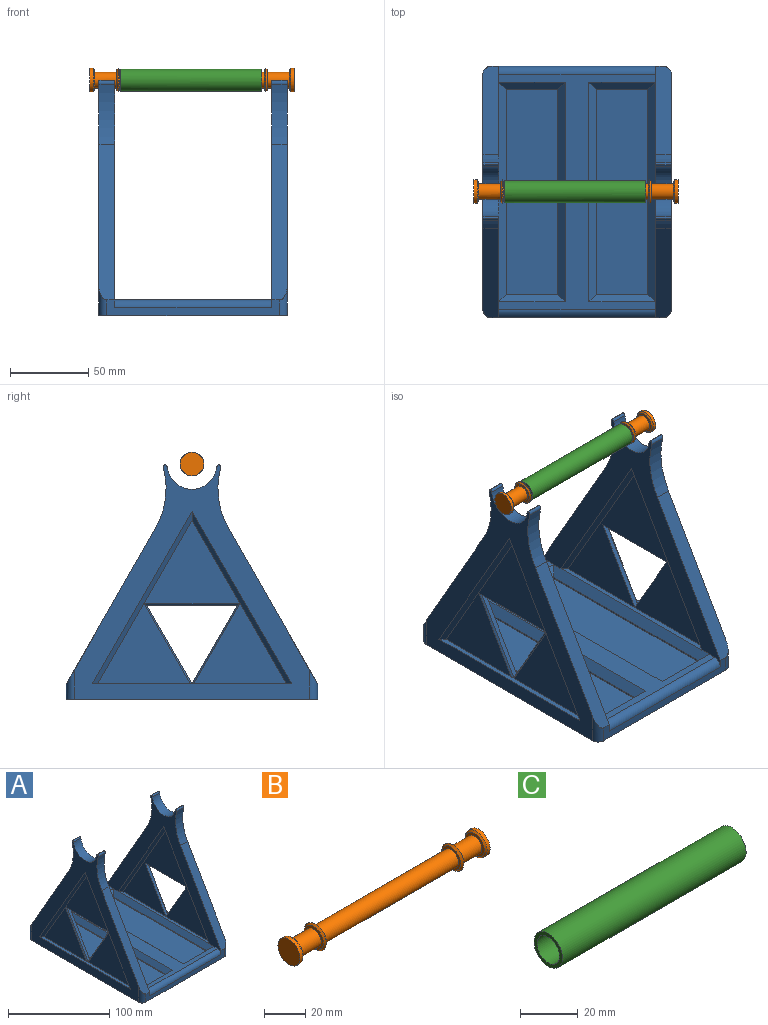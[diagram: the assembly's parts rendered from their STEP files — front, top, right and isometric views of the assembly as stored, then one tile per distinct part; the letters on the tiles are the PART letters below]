
ASSEMBLY  parts=3 mates=2
PART A: 82 faces, bbox 120x160x149.8 mm
  f0: plane 127.02x3mm, normal (0,0,1), area 370.7mm2, adj f25,f26,f27,f73
  f1: plane 127.02x3mm, normal (0,0,1), area 370.7mm2, adj f52,f53,f54,f78
  f2: plane 150x100mm, normal (0,0,1), area 3100mm2, adj f10,f41,f72,f74,f75,f76,f77,f79
  f3: plane 127.02x4mm, normal (0,0,1), area 371.8mm2, adj f13,f36,f51,f55,f56,f58,f59
  f4: plane 58.89x51mm, normal (1,0,0), area 1501.7mm2, adj f29,f32,f35
  f5: plane 61.2x53mm, normal (1,0,0), area 1621.8mm2, adj f28,f29,f30
  f6: plane 57.74x3mm, normal (0,0,-1), area 173.2mm2, adj f7,f8,f25,f30
  f7: plane 50x28.87mm, normal (0,-0.87,0.5), area 173.2mm2, adj f6,f8,f25,f32
  f8: plane 50x28.87mm, normal (0,0.87,0.5), area 173.2mm2, adj f6,f7,f25,f31
  f9: plane 150x149.84mm, normal (1,0,0), area 5795.8mm2, adj f14,f15,f16,f17,f18,f19,f20,f21
  f10: plane 160x144.84mm, normal (-1,0,0), area 4350.2mm2, adj f2,f11,f12,f15,f16,f17,f18,f19
  f11: plane 110x10mm, normal (0,-1,0), area 600mm2, adj f10,f14,f15,f33,f41,f42,f60,f81
  f12: plane 110x10mm, normal (0,1,0), area 600mm2, adj f10,f14,f16,f34,f41,f43,f61,f80
  f13: plane 150x149.84mm, normal (-1,0,0), area 5795.8mm2, adj f3,f14,f42,f43,f44,f45,f46,f47
  f14: plane 160x120mm, normal (0,0,-1), area 19178.5mm2, adj f9,f11,f12,f13,f33,f34,f60,f61
  f15: plane 99x56.57mm, normal (0,-0.87,0.5), area 1129.4mm2, adj f9,f10,f11,f19,f33
  f16: plane 99x56.57mm, normal (0,0.87,0.5), area 1129.4mm2, adj f9,f10,f12,f17,f34
  f17: cylinder r=50mm len=38.48mm, axis (1,0,0), area 398.7mm2, adj f9,f10,f16,f21
  f18: cylinder r=16mm len=31.8mm, axis (1,0,0), area 467mm2, adj f9,f10,f20,f23
  f19: cylinder r=50mm len=38.48mm, axis (1,0,0), area 398.7mm2, adj f9,f10,f15,f22
  f20: cylinder r=2mm len=10mm, axis (1,0,0), area 21.1mm2, adj f9,f10,f18,f21
  f21: cylinder r=2mm len=10mm, axis (1,0,0), area 28.6mm2, adj f9,f10,f17,f20
  f22: cylinder r=2mm len=10mm, axis (1,0,0), area 28.6mm2, adj f9,f10,f19,f23
  f23: cylinder r=2mm len=10mm, axis (1,0,0), area 21.1mm2, adj f9,f10,f18,f22
  f24: plane 58.89x51mm, normal (1,0,0), area 1501.7mm2, adj f28,f31,f35
  f25: plane 120.09x104mm, normal (-1,0,0), area 4801.2mm2, adj f0,f6,f7,f8,f26,f27
  f26: plane 110x63.51mm, normal (-0.71,-0.61,-0.35), area 524.2mm2, adj f0,f10,f25,f27
  f27: plane 110x63.51mm, normal (-0.71,0.61,-0.35), area 524.2mm2, adj f0,f10,f25,f26
  f28: plane 110x63.51mm, normal (0.71,0.61,-0.35), area 524.2mm2, adj f5,f9,f24,f29,f35
  f29: plane 110x63.51mm, normal (0.71,-0.61,-0.35), area 524.2mm2, adj f4,f5,f9,f28,f35
  f30: plane 61.2x1mm, normal (0.71,0,-0.71), area 84.1mm2, adj f5,f6,f31,f32
  f31: plane 51x30.6mm, normal (0.71,0.61,0.35), area 82.5mm2, adj f8,f24,f30,f35
  f32: plane 51x30.6mm, normal (0.71,-0.61,0.35), area 82.5mm2, adj f4,f7,f30,f35
  f33: cylinder r=5mm len=18.75mm, axis (0,0,-1), area 103.5mm2, adj f9,f11,f14,f15
  f34: cylinder r=5mm len=18.75mm, axis (0,0,1), area 103.5mm2, adj f9,f12,f14,f16
  f35: plane 127.02x4mm, normal (0,0,1), area 371.8mm2, adj f4,f9,f24,f28,f29,f31,f32
  f36: plane 58.89x51mm, normal (-1,0,0), area 1501.7mm2, adj f3,f56,f59
  f37: plane 61.2x53mm, normal (-1,0,0), area 1621.8mm2, adj f55,f56,f57
  f38: plane 57.74x3mm, normal (0,0,-1), area 173.2mm2, adj f39,f40,f52,f57
  f39: plane 50x28.87mm, normal (0,-0.87,0.5), area 173.2mm2, adj f38,f40,f52,f59
  f40: plane 50x28.87mm, normal (0,0.87,0.5), area 173.2mm2, adj f38,f39,f52,f58
  f41: plane 160x144.84mm, normal (1,0,0), area 4350.2mm2, adj f2,f11,f12,f42,f43,f44,f45,f46
  f42: plane 99x56.57mm, normal (0,-0.87,0.5), area 1129.4mm2, adj f11,f13,f41,f46,f60
  f43: plane 99x56.57mm, normal (0,0.87,0.5), area 1129.4mm2, adj f12,f13,f41,f44,f61
  f44: cylinder r=50mm len=38.48mm, axis (-1,0,0), area 398.7mm2, adj f13,f41,f43,f48
  f45: cylinder r=16mm len=31.8mm, axis (-1,0,0), area 467mm2, adj f13,f41,f47,f50
  f46: cylinder r=50mm len=38.48mm, axis (-1,0,0), area 398.7mm2, adj f13,f41,f42,f49
  f47: cylinder r=2mm len=10mm, axis (-1,0,0), area 21.1mm2, adj f13,f41,f45,f48
  f48: cylinder r=2mm len=10mm, axis (-1,0,0), area 28.6mm2, adj f13,f41,f44,f47
  f49: cylinder r=2mm len=10mm, axis (-1,0,0), area 28.6mm2, adj f13,f41,f46,f50
  f50: cylinder r=2mm len=10mm, axis (-1,0,0), area 21.1mm2, adj f13,f41,f45,f49
  f51: plane 58.89x51mm, normal (-1,0,0), area 1501.7mm2, adj f3,f55,f58
  f52: plane 120.09x104mm, normal (1,0,0), area 4801.2mm2, adj f1,f38,f39,f40,f53,f54
  f53: plane 110x63.51mm, normal (0.71,-0.61,-0.35), area 524.2mm2, adj f1,f41,f52,f54
  f54: plane 110x63.51mm, normal (0.71,0.61,-0.35), area 524.2mm2, adj f1,f41,f52,f53
  f55: plane 110x63.51mm, normal (-0.71,0.61,-0.35), area 524.2mm2, adj f3,f13,f37,f51,f56
  f56: plane 110x63.51mm, normal (-0.71,-0.61,-0.35), area 524.2mm2, adj f3,f13,f36,f37,f55
  f57: plane 61.2x1mm, normal (-0.71,0,-0.71), area 84.1mm2, adj f37,f38,f58,f59
  f58: plane 51x30.6mm, normal (-0.71,0.61,0.35), area 82.5mm2, adj f3,f40,f51,f57
  f59: plane 51x30.6mm, normal (-0.71,-0.61,0.35), area 82.5mm2, adj f3,f36,f39,f57
  f60: cylinder r=5mm len=18.75mm, axis (0,0,-1), area 103.5mm2, adj f11,f13,f14,f42
  f61: cylinder r=5mm len=18.75mm, axis (0,0,1), area 103.5mm2, adj f12,f13,f14,f43
  f62: plane 32.5x1mm, normal (0,1,0), area 32.5mm2, adj f63,f65,f66,f72
  f63: plane 130x1mm, normal (-1,0,0), area 130mm2, adj f62,f64,f66,f73
  f64: plane 32.5x1mm, normal (0,-1,0), area 32.5mm2, adj f63,f65,f66,f75
  f65: plane 130x1mm, normal (1,0,0), area 130mm2, adj f62,f64,f66,f74
  f66: plane 130x32.5mm, normal (0,0,1), area 4225mm2, adj f62,f63,f64,f65
  f67: plane 32.5x1mm, normal (0,1,0), area 32.5mm2, adj f68,f70,f71,f76
  f68: plane 130x1mm, normal (-1,0,0), area 130mm2, adj f67,f69,f71,f77
  f69: plane 32.5x1mm, normal (0,-1,0), area 32.5mm2, adj f68,f70,f71,f79
  f70: plane 130x1mm, normal (1,0,0), area 130mm2, adj f67,f69,f71,f78
  f71: plane 130x32.5mm, normal (0,0,1), area 4225mm2, adj f67,f68,f69,f70
  f72: plane 42.5x5mm, normal (0,0.71,0.71), area 265.2mm2, adj f2,f62,f73,f74
  f73: plane 140x5mm, normal (-0.71,0,0.71), area 954.6mm2, adj f0,f10,f63,f72,f75
  f74: plane 140x5mm, normal (0.71,0,0.71), area 954.6mm2, adj f2,f65,f72,f75
  f75: plane 42.5x5mm, normal (0,-0.71,0.71), area 265.2mm2, adj f2,f64,f73,f74
  f76: plane 42.5x5mm, normal (0,0.71,0.71), area 265.2mm2, adj f2,f67,f77,f78
  f77: plane 140x5mm, normal (-0.71,0,0.71), area 954.6mm2, adj f2,f68,f76,f79
  f78: plane 140x5mm, normal (0.71,0,0.71), area 954.6mm2, adj f1,f41,f70,f76,f79
  f79: plane 42.5x5mm, normal (0,-0.71,0.71), area 265.2mm2, adj f2,f69,f77,f78
  f80: cylinder r=5mm len=100mm, axis (-1,0,0), area 785.4mm2, adj f2,f10,f12,f41
  f81: cylinder r=5mm len=100mm, axis (1,0,0), area 785.4mm2, adj f2,f10,f11,f41
PART B: 19 faces, bbox 130x15x15 mm
  f0: cylinder r=5mm len=92mm, axis (1,0,0), area 2890.3mm2, adj f2,f7
  f1: cylinder r=5mm len=14mm, axis (1,0,0), area 439.8mm2, adj f3,f6
  f2: plane 13x13mm, normal (-1,0,0), area 54.2mm2, adj f0,f18
  f3: plane 13x13mm, normal (1,0,0), area 54.2mm2, adj f1,f17
  f4: plane 15x15mm, normal (1,0,0), area 176.7mm2, adj f5
  f5: cylinder r=7.5mm len=15mm, axis (-1,0,0), area 94.2mm2, adj f4,f16
  f6: plane 13x13mm, normal (-1,0,0), area 54.2mm2, adj f1,f16
  f7: plane 13x13mm, normal (1,0,0), area 54.2mm2, adj f0,f14
  f8: plane 13x13mm, normal (-1,0,0), area 54.2mm2, adj f9,f15
  f9: cylinder r=5mm len=14mm, axis (1,0,0), area 439.8mm2, adj f8,f12
  f10: plane 15x15mm, normal (-1,0,0), area 176.7mm2, adj f11
  f11: cylinder r=7.5mm len=15mm, axis (1,0,0), area 94.2mm2, adj f10,f13
  f12: plane 13x13mm, normal (1,0,0), area 54.2mm2, adj f9,f13
  f13: cone r=6.5mm half-angle=45deg, axis (-1,0,0), area 62.2mm2, adj f11,f12
  f14: cone r=7.5mm half-angle=45deg, axis (-1,0,0), area 62.2mm2, adj f7,f15
  f15: cone r=6.5mm half-angle=45deg, axis (1,0,0), area 62.2mm2, adj f8,f14
  f16: cone r=7.5mm half-angle=45deg, axis (1,0,0), area 62.2mm2, adj f5,f6
  f17: cone r=7.5mm half-angle=45deg, axis (-1,0,0), area 62.2mm2, adj f3,f18
  f18: cone r=6.5mm half-angle=45deg, axis (1,0,0), area 62.2mm2, adj f2,f17
PART C: 4 faces, bbox 90x14x14 mm
  f0: plane 14x14mm, normal (-1,0,0), area 58.9mm2, adj f1,f2
  f1: cylinder r=7mm len=90mm, axis (1,0,0), area 3958.4mm2, adj f0,f3
  f2: cylinder r=5.5mm len=90mm, axis (1,0,0), area 3110.2mm2, adj f0,f3
  f3: plane 14x14mm, normal (1,0,0), area 58.9mm2, adj f1,f2
PLACE A t=(97.64,-26.51,46.23)mm
PLACE B t=(96.94,-26.51,33.32)mm
PLACE C t=(96.45,-26.51,33.32)mm
MATE cylindrical B.f0 <-> C.f1  axis (1,0,0) through (96.94,-26.51,186.23)mm
MATE cylindrical A.f45 <-> B.f0  axis (-1,0,0) through (42.64,-26.51,186.23)mm
